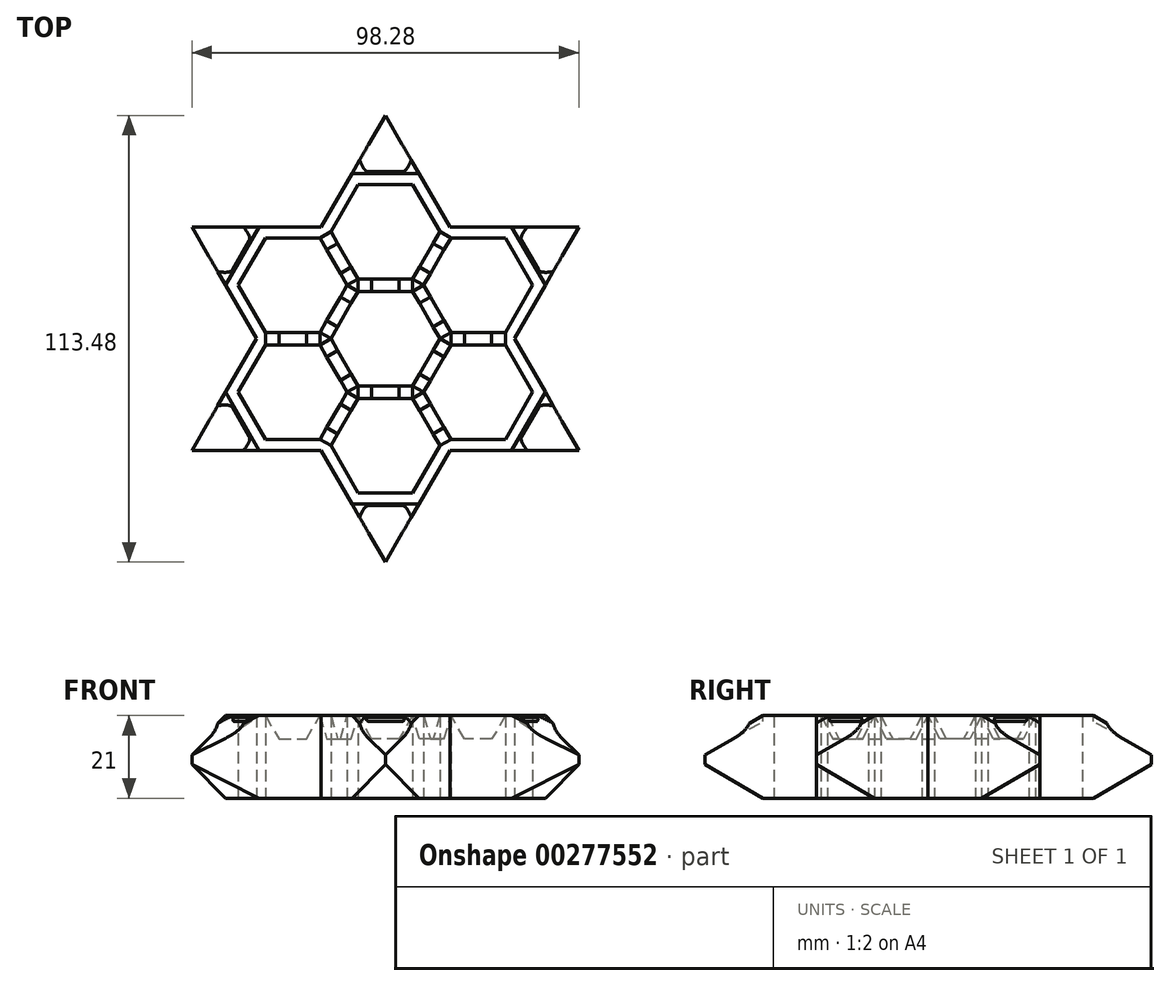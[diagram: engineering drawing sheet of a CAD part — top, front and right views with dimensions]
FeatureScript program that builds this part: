
annotation { "Feature Type Name" : "Feature", "Feature Type Description" : "" }
export const myFeature = defineFeature(function(context is Context, id is Id, definition is map)
    precondition{}
    {
        {
            assignVariable(context, id + "F0", {"variableType" : VariableType.LENGTH, "name" : "DICE_HEIGHT", "lengthValue" : 20 * mm});
        }
        {
            assignVariable(context, id + "F1", {"variableType" : VariableType.LENGTH, "name" : "WALL_THICNESS", "lengthValue" : 3.2 * mm});
        }
        {
            assignVariable(context, id + "F2", {"variableType" : VariableType.LENGTH, "name" : "BOTTOM_ENGRAVE", "lengthValue" : 1 * mm});
        }
        {
            var Q0;
            Q0=qCreatedBy(makeId("Top.planeOp"),FACE);
            var sketch = newSketch(context, id + "F3", { "sketchPlane" : qUnion([Q0])});
            skCircle(sketch, "E0.cCircle", {"center": v(0, 0) * mm, "radius": 23.56 * mm, "construction": true});
            skLineSegment(sketch, "E0.0", {"start": v(23.56, 13.6) * mm, "end": v(23.56, -13.6) * mm, "construction": true});
            skLineSegment(sketch, "E0.1", {"start": v(23.56, -13.6) * mm, "end": v(0, -27.2) * mm, "construction": true});
            skLineSegment(sketch, "E0.2", {"start": v(0, -27.2) * mm, "end": v(-23.56, -13.6) * mm, "construction": true});
            skLineSegment(sketch, "E0.3", {"start": v(-23.56, -13.6) * mm, "end": v(-23.56, 13.6) * mm, "construction": true});
            skLineSegment(sketch, "E0.4", {"start": v(-23.56, 13.6) * mm, "end": v(0, 27.2) * mm, "construction": true});
            skLineSegment(sketch, "E0.5", {"start": v(0, 27.2) * mm, "end": v(23.56, 13.6) * mm, "construction": true});
            skPoint(sketch, "E0.0.midPoint", {"position": v(23.56, 0) * mm});
            skCircle(sketch, "E1", {"center": v(0, 0) * mm, "radius": 27.2 * mm, "construction": true});
            skSolve(sketch);
        }
        {
            var Q0;
            Q0=qCreatedBy(makeId("Top.planeOp"),FACE);
            var sketch = newSketch(context, id + "F4", { "sketchPlane" : qUnion([Q0])});
            skCircle(sketch, "E2.cCircle", {"center": v(0, 0) * mm, "radius": 12 * mm, "construction": true});
            skLineSegment(sketch, "E2.0", {"start": v(-6.93, 12) * mm, "end": v(6.93, 12) * mm});
            skLineSegment(sketch, "E2.1", {"start": v(6.93, 12) * mm, "end": v(13.86, 0) * mm});
            skLineSegment(sketch, "E2.2", {"start": v(13.86, 0) * mm, "end": v(6.93, -12) * mm});
            skLineSegment(sketch, "E2.3", {"start": v(6.93, -12) * mm, "end": v(-6.93, -12) * mm});
            skLineSegment(sketch, "E2.4", {"start": v(-6.93, -12) * mm, "end": v(-13.86, 0) * mm});
            skLineSegment(sketch, "E2.5", {"start": v(-13.86, 0) * mm, "end": v(-6.93, 12) * mm});
            skPoint(sketch, "E2.0.midPoint", {"position": v(0, 12) * mm});
            skCircle(sketch, "E3.cCircle", {"center": v(0, 27.2) * mm, "radius": 12 * mm, "construction": true});
            skLineSegment(sketch, "E3.0", {"start": v(-6.93, 39.2) * mm, "end": v(6.93, 39.2) * mm});
            skLineSegment(sketch, "E3.1", {"start": v(6.93, 39.2) * mm, "end": v(13.86, 27.2) * mm});
            skLineSegment(sketch, "E3.2", {"start": v(13.86, 27.2) * mm, "end": v(6.93, 15.2) * mm});
            skLineSegment(sketch, "E3.3", {"start": v(6.93, 15.2) * mm, "end": v(-6.93, 15.2) * mm});
            skLineSegment(sketch, "E3.4", {"start": v(-6.93, 15.2) * mm, "end": v(-13.86, 27.2) * mm});
            skLineSegment(sketch, "E3.5", {"start": v(-13.86, 27.2) * mm, "end": v(-6.93, 39.2) * mm});
            skPoint(sketch, "E3.0.midPoint", {"position": v(0, 39.2) * mm});
            skCircle(sketch, "E4.cCircle", {"center": v(23.56, 13.6) * mm, "radius": 12 * mm, "construction": true});
            skLineSegment(sketch, "E4.0", {"start": v(16.63, 25.6) * mm, "end": v(30.48, 25.6) * mm});
            skLineSegment(sketch, "E4.1", {"start": v(30.48, 25.6) * mm, "end": v(37.41, 13.6) * mm});
            skLineSegment(sketch, "E4.2", {"start": v(37.41, 13.6) * mm, "end": v(30.48, 1.6) * mm});
            skLineSegment(sketch, "E4.3", {"start": v(30.48, 1.6) * mm, "end": v(16.63, 1.6) * mm});
            skLineSegment(sketch, "E4.4", {"start": v(16.63, 1.6) * mm, "end": v(9.7, 13.6) * mm});
            skLineSegment(sketch, "E4.5", {"start": v(9.7, 13.6) * mm, "end": v(16.63, 25.6) * mm});
            skPoint(sketch, "E4.0.midPoint", {"position": v(23.56, 25.6) * mm});
            skCircle(sketch, "E5.cCircle", {"center": v(23.56, -13.6) * mm, "radius": 12 * mm, "construction": true});
            skLineSegment(sketch, "E5.0", {"start": v(16.63, -1.6) * mm, "end": v(30.48, -1.6) * mm});
            skLineSegment(sketch, "E5.1", {"start": v(30.48, -1.6) * mm, "end": v(37.41, -13.6) * mm});
            skLineSegment(sketch, "E5.2", {"start": v(37.41, -13.6) * mm, "end": v(30.48, -25.6) * mm});
            skLineSegment(sketch, "E5.3", {"start": v(30.48, -25.6) * mm, "end": v(16.63, -25.6) * mm});
            skLineSegment(sketch, "E5.4", {"start": v(16.63, -25.6) * mm, "end": v(9.7, -13.6) * mm});
            skLineSegment(sketch, "E5.5", {"start": v(9.7, -13.6) * mm, "end": v(16.63, -1.6) * mm});
            skPoint(sketch, "E5.0.midPoint", {"position": v(23.56, -1.6) * mm});
            skCircle(sketch, "E6.cCircle", {"center": v(-23.56, 13.6) * mm, "radius": 12 * mm, "construction": true});
            skLineSegment(sketch, "E6.0", {"start": v(-30.48, 25.6) * mm, "end": v(-16.63, 25.6) * mm});
            skLineSegment(sketch, "E6.1", {"start": v(-16.63, 25.6) * mm, "end": v(-9.7, 13.6) * mm});
            skLineSegment(sketch, "E6.2", {"start": v(-9.7, 13.6) * mm, "end": v(-16.63, 1.6) * mm});
            skLineSegment(sketch, "E6.3", {"start": v(-16.63, 1.6) * mm, "end": v(-30.48, 1.6) * mm});
            skLineSegment(sketch, "E6.4", {"start": v(-30.48, 1.6) * mm, "end": v(-37.41, 13.6) * mm});
            skLineSegment(sketch, "E6.5", {"start": v(-37.41, 13.6) * mm, "end": v(-30.48, 25.6) * mm});
            skPoint(sketch, "E6.0.midPoint", {"position": v(-23.56, 25.6) * mm});
            skCircle(sketch, "E7.cCircle", {"center": v(-23.56, -13.6) * mm, "radius": 12 * mm, "construction": true});
            skLineSegment(sketch, "E7.0", {"start": v(-30.48, -1.6) * mm, "end": v(-16.63, -1.6) * mm});
            skLineSegment(sketch, "E7.1", {"start": v(-16.63, -1.6) * mm, "end": v(-9.7, -13.6) * mm});
            skLineSegment(sketch, "E7.2", {"start": v(-9.7, -13.6) * mm, "end": v(-16.63, -25.6) * mm});
            skLineSegment(sketch, "E7.3", {"start": v(-16.63, -25.6) * mm, "end": v(-30.48, -25.6) * mm});
            skLineSegment(sketch, "E7.4", {"start": v(-30.48, -25.6) * mm, "end": v(-37.41, -13.6) * mm});
            skLineSegment(sketch, "E7.5", {"start": v(-37.41, -13.6) * mm, "end": v(-30.48, -1.6) * mm});
            skPoint(sketch, "E7.0.midPoint", {"position": v(-23.56, -1.6) * mm});
            skCircle(sketch, "E8.cCircle", {"center": v(0, -27.2) * mm, "radius": 12 * mm, "construction": true});
            skLineSegment(sketch, "E8.0", {"start": v(-6.93, -15.2) * mm, "end": v(6.93, -15.2) * mm});
            skLineSegment(sketch, "E8.1", {"start": v(6.93, -15.2) * mm, "end": v(13.86, -27.2) * mm});
            skLineSegment(sketch, "E8.2", {"start": v(13.86, -27.2) * mm, "end": v(6.93, -39.2) * mm});
            skLineSegment(sketch, "E8.3", {"start": v(6.93, -39.2) * mm, "end": v(-6.93, -39.2) * mm});
            skLineSegment(sketch, "E8.4", {"start": v(-6.93, -39.2) * mm, "end": v(-13.86, -27.2) * mm});
            skLineSegment(sketch, "E8.5", {"start": v(-13.86, -27.2) * mm, "end": v(-6.93, -15.2) * mm});
            skPoint(sketch, "E8.0.midPoint", {"position": v(0, -15.2) * mm});
            skLineSegment(sketch, "E9", {"start": v(-32.76, 0) * mm, "end": v(-40.61, -13.6) * mm});
            skLineSegment(sketch, "E10", {"start": v(-40.61, -13.6) * mm, "end": v(-32.08, -28.37) * mm});
            skLineSegment(sketch, "E11", {"start": v(-16.38, -28.37) * mm, "end": v(-32.08, -28.37) * mm});
            skLineSegment(sketch, "E12", {"start": v(-23.56, -13.6) * mm, "end": v(-30.48, -25.6) * mm, "construction": true});
            skLineSegment(sketch, "E13", {"start": v(-30.48, -25.6) * mm, "end": v(-32.08, -28.37) * mm, "construction": true});
            skLineSegment(sketch, "E14", {"start": v(-37.41, -13.6) * mm, "end": v(-40.61, -13.6) * mm, "construction": true});
            skLineSegment(sketch, "E15.1.0", {"start": v(-16.38, -28.37) * mm, "end": v(-8.53, -41.97) * mm});
            skLineSegment(sketch, "E15.1.1", {"start": v(-8.53, -41.97) * mm, "end": v(8.53, -41.97) * mm});
            skLineSegment(sketch, "E15.1.2", {"start": v(16.38, -28.37) * mm, "end": v(8.53, -41.97) * mm});
            skLineSegment(sketch, "E15.2.0", {"start": v(16.38, -28.37) * mm, "end": v(32.08, -28.37) * mm});
            skLineSegment(sketch, "E15.2.1", {"start": v(32.08, -28.37) * mm, "end": v(40.61, -13.6) * mm});
            skLineSegment(sketch, "E15.2.2", {"start": v(32.76, 0) * mm, "end": v(40.61, -13.6) * mm});
            skLineSegment(sketch, "E15.3.0", {"start": v(32.76, 0) * mm, "end": v(40.61, 13.6) * mm});
            skLineSegment(sketch, "E15.3.1", {"start": v(40.61, 13.6) * mm, "end": v(32.08, 28.37) * mm});
            skLineSegment(sketch, "E15.3.2", {"start": v(16.38, 28.37) * mm, "end": v(32.08, 28.37) * mm});
            skLineSegment(sketch, "E15.4.0", {"start": v(16.38, 28.37) * mm, "end": v(8.53, 41.97) * mm});
            skLineSegment(sketch, "E15.4.1", {"start": v(8.53, 41.97) * mm, "end": v(-8.53, 41.97) * mm});
            skLineSegment(sketch, "E15.4.2", {"start": v(-16.38, 28.37) * mm, "end": v(-8.53, 41.97) * mm});
            skLineSegment(sketch, "E15.5.0", {"start": v(-16.38, 28.37) * mm, "end": v(-32.08, 28.37) * mm});
            skLineSegment(sketch, "E15.5.1", {"start": v(-32.08, 28.37) * mm, "end": v(-40.61, 13.6) * mm});
            skLineSegment(sketch, "E15.5.2", {"start": v(-32.76, 0) * mm, "end": v(-40.61, 13.6) * mm});
            skSolve(sketch);
        }
        {
            var Q0;
            Q0=makeQuery(id+"F4.imprint","IMPRINT",FACE,{"disambiguationData":[TD([[makeQuery(id+"F4.imprint","IMPRINT",EDGE,{"derivedFrom":sQuery(id+"F4.wireOp",EDGE,"E2.0")}),1.0]])]});
            extrude(context, id + "F5", {"entities" : qUnion([Q0]), "depth" : getVariable(context, 'DICE_HEIGHT'), "offsetDistance" : 25 * mm, "hasSecondDirection" : true, "secondDirectionOppositeDirection" : true, "secondDirectionDepth" : getVariable(context, 'BOTTOM_ENGRAVE')});
        }
        {
            var Q0;
            Q0=qCreatedBy(makeId("Front.planeOp"),FACE);
            var sketch = newSketch(context, id + "F6", { "sketchPlane" : qUnion([Q0])});
            skLineSegment(sketch, "E16", {"start": v(-30.48, 20) * mm, "end": v(-27.02, 14) * mm});
            skLineSegment(sketch, "E17", {"start": v(-27.02, 14) * mm, "end": v(-20.1, 14) * mm});
            skLineSegment(sketch, "E18", {"start": v(-20.1, 14) * mm, "end": v(-16.63, 20) * mm});
            skLineSegment(sketch, "E19", {"start": v(-16.63, 20) * mm, "end": v(-30.48, 20) * mm});
            skLineSegment(sketch, "E20", {"start": v(-23.56, 20) * mm, "end": v(-23.56, 14) * mm, "construction": true});
            skLineSegment(sketch, "E21", {"start": v(0, 0) * mm, "end": v(0, 20) * mm, "construction": true});
            skSolve(sketch);
        }
        {
            var Q0;
            Q0=makeQuery(id+"F6.imprint","IMPRINT",FACE,{"disambiguationData":[TD([[makeQuery(id+"F6.imprint","IMPRINT",EDGE,{"derivedFrom":sQuery(id+"F6.wireOp",EDGE,"E16")}),1.0]])]});
            extrude(context, id + "F7", {"entities" : qUnion([Q0]), "endBound" : BoundingType.SYMMETRIC, "depth" : getVariable(context, 'WALL_THICNESS'), "offsetDistance" : 25 * mm});
        }
        {
            var Q0;
            Q0=sQuery(id+"F4.wireOp",EDGE,"E7.0");
            cPoint(context, id + "F8", {"entities" : qUnion([Q0]), "parameter" : 0.5});
        }
        {
            var Q0;
            Q0=makeQuery(id+"F7.opExtrude","SWEPT_BODY",BODY,{"disambiguationData":[OSD([sQuery(id+"F6.wireOp",EDGE,"E16"),sQuery(id+"F6.wireOp",EDGE,"E17"),sQuery(id+"F6.wireOp",EDGE,"E18"),sQuery(id+"F6.wireOp",EDGE,"E19")])]});
            var Q1;
            Q1 = qCreatedBy(id + "F8" ,VERTEX);
            var Q2;
            Q2=sQuery(id+"F4.wireOp",VERTEX,"E8.0.midPoint");
            transform(context, id + "F9", {"entities" : qUnion([Q0]), "transformType" : TransformType.TRANSLATION_ENTITY, "oppositeDirectionEntity" : false, "transformLine" : qUnion([Q1, Q2]), "makeCopy" : true});
        }
        {
            var Q0;
            Q0=makeQuery(id+"F7.opExtrude","SWEPT_BODY",BODY,{"disambiguationData":[OSD([sQuery(id+"F6.wireOp",EDGE,"E16"),sQuery(id+"F6.wireOp",EDGE,"E17"),sQuery(id+"F6.wireOp",EDGE,"E18"),sQuery(id+"F6.wireOp",EDGE,"E19")])]});
            var Q1;
            Q1=sQuery(id+"F6.wireOp",EDGE,"E21");
            circularPattern(context, id + "F10", {"operationType" : NewBodyOperationType.REMOVE, "entities" : qUnion([Q0]), "axis" : qUnion([Q1]), "angle" : 360 * degree, "instanceCount" : 6, "equalSpace" : true});
        }
        {
            var Q0;
            Q0=makeQuery(id+"F9.opPattern","COPY",BODY,{"derivedFrom":makeQuery(id+"F7.opExtrude","SWEPT_BODY",BODY,{"disambiguationData":[OSD([sQuery(id+"F6.wireOp",EDGE,"E16"),sQuery(id+"F6.wireOp",EDGE,"E17"),sQuery(id+"F6.wireOp",EDGE,"E18"),sQuery(id+"F6.wireOp",EDGE,"E19")])]}),"instanceName":"1"});
            var Q1;
            Q1=sQuery(id+"F6.wireOp",EDGE,"E21");
            circularPattern(context, id + "F11", {"operationType" : NewBodyOperationType.REMOVE, "entities" : qUnion([Q0]), "axis" : qUnion([Q1]), "angle" : 360 * degree, "instanceCount" : 6, "equalSpace" : true});
        }
        {
            var Q0;
            Q0=makeQuery(id+"F5.opExtrude","SWEPT_FACE",FACE,{"disambiguationData":[OSD([sQuery(id+"F4.wireOp",EDGE,"E15.1.1")])]});
            var sketch = newSketch(context, id + "F12", { "sketchPlane" : qUnion([Q0])});
            skLineSegment(sketch, "E22", {"start": v(-4.26, 19) * mm, "end": v(4.26, 19) * mm, "construction": true});
            skPoint(sketch, "E23", {"position": v(0, 19) * mm});
            skLineSegment(sketch, "E24", {"start": v(-8.53, 20) * mm, "end": v(0, 20) * mm, "construction": true});
            skPoint(sketch, "E25", {"position": v(-4.26, 20) * mm});
            skArc(sketch, "E26.0.startCap", {"start": v(-4.26, 18.5) * mm, "mid": v(-4.76, 19) * mm, "end": v(-4.26, 19.5) * mm});
            skArc(sketch, "E26.0.endCap", {"start": v(4.26, 19.5) * mm, "mid": v(4.76, 19) * mm, "end": v(4.26, 18.5) * mm});
            skLineSegment(sketch, "E26.0.left", {"start": v(-4.26, 19.5) * mm, "end": v(4.26, 19.5) * mm});
            skLineSegment(sketch, "E26.0.right", {"start": v(-4.26, 18.5) * mm, "end": v(4.26, 18.5) * mm});
            skSolve(sketch);
        }
        {
            var Q0;
            Q0=makeQuery(id+"F12.imprint","IMPRINT",FACE,{"disambiguationData":[TD([[makeQuery(id+"F12.imprint","IMPRINT",EDGE,{"derivedFrom":sQuery(id+"F12.wireOp",EDGE,"E26.0.startCap")}),-1.0]])]});
            extrude(context, id + "F13", {"entities" : qUnion([Q0]), "endBound" : BoundingType.THROUGH_ALL, "depth" : 25 * mm, "offsetDistance" : 25 * mm, "hasDraft" : true, "draftAngle" : 30 * degree, "draftPullDirection" : true});
        }
        {
            var Q0;
            Q0=makeQuery(id+"F13.opExtrude","SWEPT_BODY",BODY,{"disambiguationData":[OSD([sQuery(id+"F12.wireOp",EDGE,"E26.0.startCap"),sQuery(id+"F12.wireOp",EDGE,"E26.0.endCap"),sQuery(id+"F12.wireOp",EDGE,"E26.0.left"),sQuery(id+"F12.wireOp",EDGE,"E26.0.right")])]});
            var Q1;
            Q1=sQuery(id+"F6.wireOp",EDGE,"E21");
            circularPattern(context, id + "F14", {"operationType" : NewBodyOperationType.ADD, "entities" : qUnion([Q0]), "axis" : qUnion([Q1]), "angle" : 360 * degree, "instanceCount" : 6, "equalSpace" : true});
        }
    });
